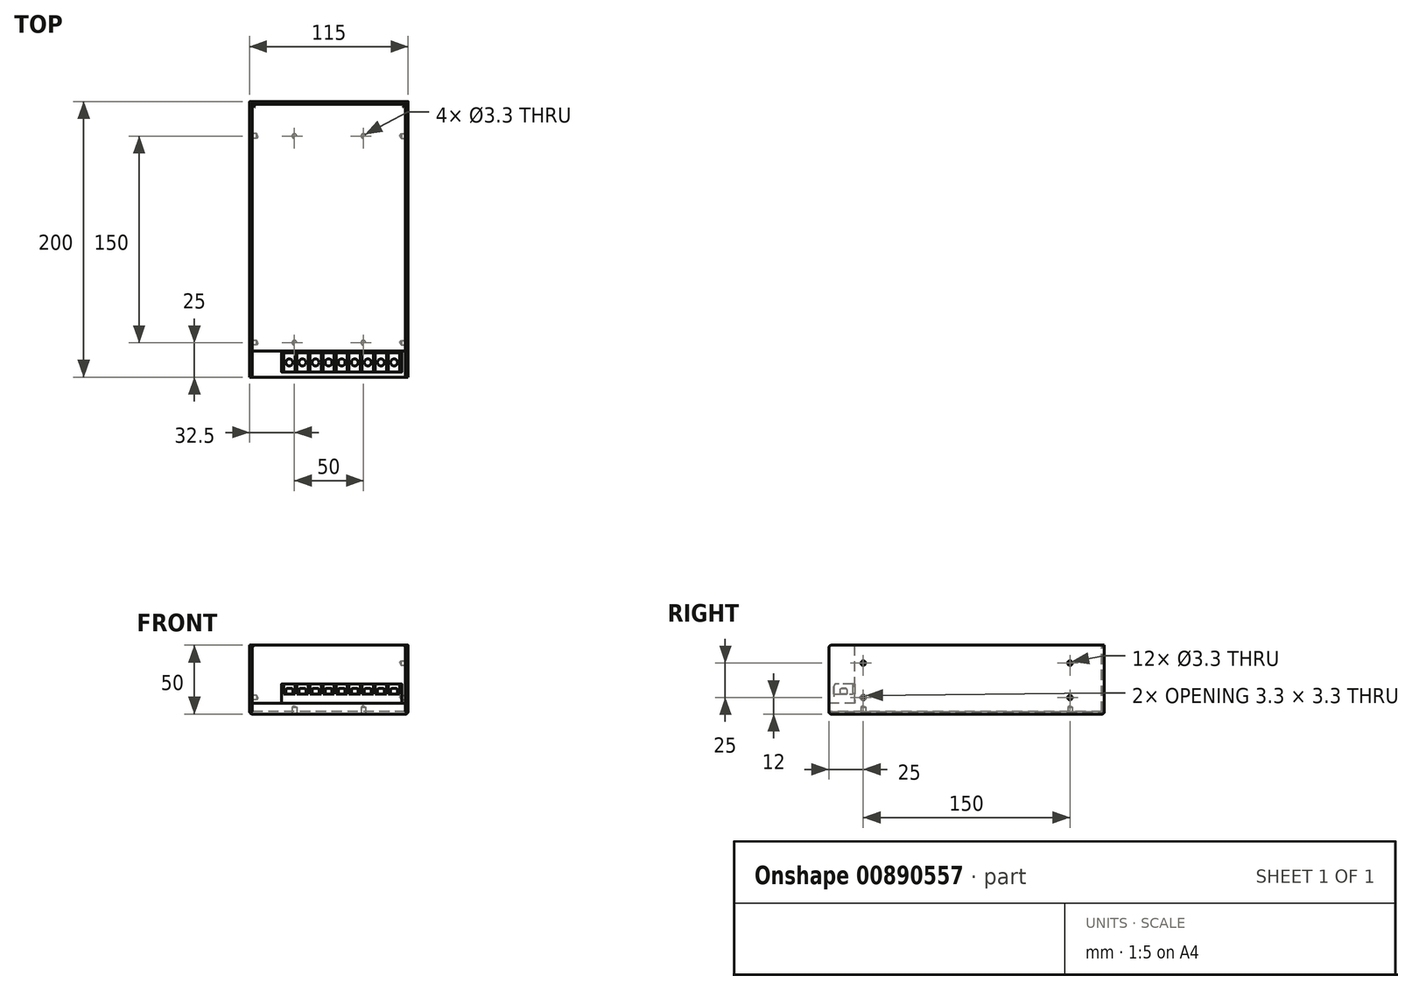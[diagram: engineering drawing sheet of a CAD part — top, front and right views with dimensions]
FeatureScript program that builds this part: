
annotation { "Feature Type Name" : "Feature", "Feature Type Description" : "" }
export const myFeature = defineFeature(function(context is Context, id is Id, definition is map)
    precondition{}
    {
        {
            var Q0;
            Q0=qCreatedBy(makeId("Front.planeOp"),FACE);
            var sketch = newSketch(context, id + "F0", { "sketchPlane" : qUnion([Q0])});
            skLineSegment(sketch, "E0.bottom", {"start": v(-57.5, 25) * mm, "end": v(0, 25) * mm});
            skLineSegment(sketch, "E0.top", {"start": v(-57.5, -25) * mm, "end": v(0, -25) * mm});
            skLineSegment(sketch, "E0.left", {"start": v(-57.5, 25) * mm, "end": v(-57.5, -25) * mm});
            skLineSegment(sketch, "E0.right", {"start": v(0, 25) * mm, "end": v(0, -25) * mm});
            skLineSegment(sketch, "E1", {"start": v(0, 0) * mm, "end": v(0, 48.13) * mm, "construction": true});
            skLineSegment(sketch, "E2", {"start": v(0, 0) * mm, "end": v(-98.9, 0) * mm, "construction": true});
            skPoint(sketch, "E2.endSnap0", {"position": v(0, 0) * mm});
            skSolve(sketch);
        }
        {
            var Q0;
            Q0=makeQuery(id+"F0.imprint","IMPRINT",FACE,{"disambiguationData":[TD([[makeQuery(id+"F0.imprint","IMPRINT",EDGE,{"derivedFrom":sQuery(id+"F0.wireOp",EDGE,"E0.bottom")}),-1.0]])]});
            extrude(context, id + "F1", {"entities" : qUnion([Q0]), "endBound" : BoundingType.SYMMETRIC, "offsetDistance" : 25 * mm, "depth" : 200 * mm});
        }
        {
            var Q0;
            Q0=makeQuery(id+"F1.opExtrude","SWEPT_FACE",FACE,{"disambiguationData":[OSD([sQuery(id+"F0.wireOp",EDGE,"E0.bottom")])]});
            var sketch = newSketch(context, id + "F2", { "sketchPlane" : qUnion([Q0])});
            skLineSegment(sketch, "E3.bottom", {"start": v(0, -100) * mm, "end": v(-55.8, -100) * mm});
            skLineSegment(sketch, "E3.top", {"start": v(0, -81) * mm, "end": v(-55.8, -81) * mm});
            skLineSegment(sketch, "E3.left", {"start": v(0, -100) * mm, "end": v(0, -81) * mm});
            skLineSegment(sketch, "E3.right", {"start": v(-55.8, -100) * mm, "end": v(-55.8, -81) * mm});
            skSolve(sketch);
        }
        {
            var Q0;
            Q0=makeQuery(id+"F2.imprint","IMPRINT",FACE,{"disambiguationData":[TD([[makeQuery(id+"F2.imprint","IMPRINT",EDGE,{"derivedFrom":sQuery(id+"F2.wireOp",EDGE,"E3.bottom")}),1.0]])]});
            extrude(context, id + "F3", {"entities" : qUnion([Q0]), "operationType" : NewBodyOperationType.REMOVE, "oppositeDirection" : true, "depth" : 42 * mm});
        }
        {
            var Q0;
            Q0=makeQuery(id+"F1.opExtrude","SWEPT_FACE",FACE,{"disambiguationData":[OSD([sQuery(id+"F0.wireOp",EDGE,"E0.bottom")])]});
            var sketch = newSketch(context, id + "F4", { "sketchPlane" : qUnion([Q0])});
            skLineSegment(sketch, "E4", {"start": v(-55.8, -100) * mm, "end": v(-55.8, 100) * mm});
            skLineSegment(sketch, "E5", {"start": v(-55.8, 100) * mm, "end": v(-55.5, 100) * mm});
            skLineSegment(sketch, "E6", {"start": v(-55.5, 100) * mm, "end": v(-55.5, 98.3) * mm});
            skLineSegment(sketch, "E7", {"start": v(-55.5, 98.3) * mm, "end": v(0, 98.3) * mm});
            skLineSegment(sketch, "E8", {"start": v(0, 98.3) * mm, "end": v(0, 98) * mm});
            skLineSegment(sketch, "E9", {"start": v(0, 98) * mm, "end": v(-55.5, 98) * mm});
            skLineSegment(sketch, "E10", {"start": v(-55.5, 98) * mm, "end": v(-55.5, -100) * mm});
            skLineSegment(sketch, "E11", {"start": v(-55.5, -100) * mm, "end": v(-55.8, -100) * mm});
            skSolve(sketch);
        }
        {
            var Q0;
            {var subQ1=sQuery(id+"F4.wireOp",EDGE,"E5");Q0=makeQuery(id+"F4.imprint","IMPRINT",FACE,{"disambiguationData":[TD([[makeQuery(id+"F4.imprint","IMPRINT",EDGE,{"derivedFrom":subQ1}),-1.0]])]});}
            var Q1;
            {var subQ0=sQuery(id+"F4.wireOp",EDGE,"E11");Q1=makeQuery(id+"F4.imprint","IMPRINT",FACE,{"disambiguationData":[TD([[makeQuery(id+"F4.imprint","IMPRINT",EDGE,{"derivedFrom":subQ0}),-1.0]])]});}
            extrude(context, id + "F5", {"entities" : qUnion([Q0, Q1]), "operationType" : NewBodyOperationType.REMOVE, "oppositeDirection" : true, "depth" : 48.3 * mm});
        }
        {
            var Q0;
            Q0=makeQuery(id+"F3.boolean.opBoolean","COPY",EDGE,{"derivedFrom":makeQuery(id+"F3.opExtrude","CAP_EDGE",EDGE,{"disambiguationData":[OSD([sQuery(id+"F2.wireOp",EDGE,"E3.top")])],"isStart":true})});
            var Q1;
            Q1=makeQuery(id+"F1.opExtrude","CAP_EDGE",EDGE,{"disambiguationData":[OSD([sQuery(id+"F0.wireOp",EDGE,"E0.top")])],"isStart":false});
            var Q2;
            Q2=makeQuery(id+"F1.opExtrude","SWEPT_EDGE",EDGE,{"disambiguationData":[OSD([sQuery(id+"F0.wireOp",EDGE,"E0.top"),sQuery(id+"F0.wireOp",EDGE,"E0.left")])]});
            var Q3;
            Q3=makeQuery(id+"F1.opExtrude","CAP_EDGE",EDGE,{"disambiguationData":[OSD([sQuery(id+"F0.wireOp",EDGE,"E0.top")])],"isStart":true});
            var Q4;
            Q4=makeQuery(id+"F1.opExtrude","CAP_EDGE",EDGE,{"disambiguationData":[OSD([sQuery(id+"F0.wireOp",EDGE,"E0.bottom")])],"isStart":false});
            var Q5;
            {var subQ0=sQuery(id+"F0.wireOp",EDGE,"E0.bottom");var subQ1=sQuery(id+"F0.wireOp",EDGE,"E0.left");Q5=makeQuery(id+"F5.boolean.opBoolean","SPLIT",EDGE,{"disambiguationData":[TD([makeQuery(id+"F1.opExtrude","SWEPT_FACE",FACE,{"disambiguationData":[OSD([subQ1])]})])],"derivedFrom":makeQuery(id+"F1.opExtrude","CAP_EDGE",EDGE,{"disambiguationData":[OSD([subQ0])],"isStart":true})});}
            var Q6;
            Q6=makeQuery(id+"F5.boolean.opBoolean","COPY",EDGE,{"derivedFrom":makeQuery(id+"F5.opExtrude","CAP_EDGE",EDGE,{"disambiguationData":[OSD([sQuery(id+"F4.wireOp",EDGE,"E6")])],"isStart":true})});
            var Q7;
            Q7=makeQuery(id+"F5.boolean.opBoolean","COPY",EDGE,{"derivedFrom":makeQuery(id+"F5.opExtrude","CAP_EDGE",EDGE,{"disambiguationData":[OSD([sQuery(id+"F4.wireOp",EDGE,"E9")])],"isStart":true})});
            var Q8;
            Q8=makeQuery(id+"F5.boolean.opBoolean","COPY",EDGE,{"derivedFrom":makeQuery(id+"F5.opExtrude","CAP_EDGE",EDGE,{"disambiguationData":[OSD([sQuery(id+"F4.wireOp",EDGE,"E10")])],"isStart":true})});
            fillet(context, id + "F6", {"entities" : qUnion([Q0, Q1, Q2, Q3, Q4, Q5, Q6, Q7, Q8]), "radius" : 2 * mm, "tangentPropagation" : true, "allowEdgeOverflow" : false});
        }
        {
            var Q0;
            Q0=makeQuery(id+"F1.opExtrude","SWEPT_BODY",BODY,{"disambiguationData":[OSD([sQuery(id+"F0.wireOp",EDGE,"E0.bottom"),sQuery(id+"F0.wireOp",EDGE,"E0.top"),sQuery(id+"F0.wireOp",EDGE,"E0.left"),sQuery(id+"F0.wireOp",EDGE,"E0.right")])]});
            var Q1;
            Q1=qCreatedBy(makeId("Right.planeOp"),FACE);
            mirror(context, id + "F7", {"operationType" : NewBodyOperationType.ADD, "entities" : qUnion([Q0]), "mirrorPlane" : qUnion([Q1])});
        }
        {
            var Q0;
            {var subQ0=makeQuery(id+"F3.boolean.opBoolean","COPY",FACE,{"derivedFrom":makeQuery(id+"F3.opExtrude","CAP_FACE",FACE,{"disambiguationData":[OSD([sQuery(id+"F2.wireOp",EDGE,"E3.bottom"),sQuery(id+"F2.wireOp",EDGE,"E3.top"),sQuery(id+"F2.wireOp",EDGE,"E3.left"),sQuery(id+"F2.wireOp",EDGE,"E3.right")])],"isStart":false})});Q0=makeQuery(id+"F7.boolean.opBoolean","MERGE",FACE,{"derivedFrom":[subQ0,makeQuery(id+"F7.opPattern","COPY",FACE,{"derivedFrom":subQ0,"instanceName":"1"})]});}
            var sketch = newSketch(context, id + "F8", { "sketchPlane" : qUnion([Q0])});
            skLineSegment(sketch, "E12.bottom", {"start": v(-34.2, -81) * mm, "end": v(52.8, -81) * mm});
            skLineSegment(sketch, "E12.top", {"start": v(-34.2, -96.3) * mm, "end": v(52.8, -96.3) * mm});
            skLineSegment(sketch, "E12.left", {"start": v(-34.2, -81) * mm, "end": v(-34.2, -96.3) * mm});
            skLineSegment(sketch, "E12.right", {"start": v(52.8, -81) * mm, "end": v(52.8, -96.3) * mm});
            skSolve(sketch);
        }
        {
            var Q0;
            Q0=makeQuery(id+"F8.imprint","IMPRINT",FACE,{"disambiguationData":[TD([[makeQuery(id+"F8.imprint","IMPRINT",EDGE,{"derivedFrom":sQuery(id+"F8.wireOp",EDGE,"E12.bottom")}),1.0]])]});
            extrude(context, id + "F9", {"entities" : qUnion([Q0]), "depth" : 14 * mm});
        }
        {
            var Q0;
            Q0=makeQuery(id+"F9.opExtrude","CAP_FACE",FACE,{"disambiguationData":[OSD([sQuery(id+"F8.wireOp",EDGE,"E12.bottom"),sQuery(id+"F8.wireOp",EDGE,"E12.top"),sQuery(id+"F8.wireOp",EDGE,"E12.left"),sQuery(id+"F8.wireOp",EDGE,"E12.right")])],"isStart":false});
            var sketch = newSketch(context, id + "F10", { "sketchPlane" : qUnion([Q0])});
            skLineSegment(sketch, "E13", {"start": v(-32.8, -96.3) * mm, "end": v(-32.8, -82.3) * mm});
            skLineSegment(sketch, "E14", {"start": v(-32.8, -82.3) * mm, "end": v(-24.6, -82.3) * mm});
            skLineSegment(sketch, "E15", {"start": v(-24.6, -82.3) * mm, "end": v(-24.6, -96.3) * mm});
            skLineSegment(sketch, "E16", {"start": v(-24.6, -96.3) * mm, "end": v(-32.8, -96.3) * mm});
            skLineSegment(sketch, "E17.1.0.0", {"start": v(-23.3, -96.3) * mm, "end": v(-23.3, -82.3) * mm});
            skLineSegment(sketch, "E17.1.0.1", {"start": v(-15.1, -96.3) * mm, "end": v(-23.3, -96.3) * mm});
            skLineSegment(sketch, "E17.1.0.2", {"start": v(-15.1, -82.3) * mm, "end": v(-15.1, -96.3) * mm});
            skLineSegment(sketch, "E17.1.0.3", {"start": v(-23.3, -82.3) * mm, "end": v(-15.1, -82.3) * mm});
            skLineSegment(sketch, "E17.2.0.0", {"start": v(-13.8, -96.3) * mm, "end": v(-13.8, -82.3) * mm});
            skLineSegment(sketch, "E17.2.0.1", {"start": v(-5.6, -96.3) * mm, "end": v(-13.8, -96.3) * mm});
            skLineSegment(sketch, "E17.2.0.2", {"start": v(-5.6, -82.3) * mm, "end": v(-5.6, -96.3) * mm});
            skLineSegment(sketch, "E17.2.0.3", {"start": v(-13.8, -82.3) * mm, "end": v(-5.6, -82.3) * mm});
            skLineSegment(sketch, "E17.3.0.0", {"start": v(-4.3, -96.3) * mm, "end": v(-4.3, -82.3) * mm});
            skLineSegment(sketch, "E17.3.0.1", {"start": v(3.9, -96.3) * mm, "end": v(-4.3, -96.3) * mm});
            skLineSegment(sketch, "E17.3.0.2", {"start": v(3.9, -82.3) * mm, "end": v(3.9, -96.3) * mm});
            skLineSegment(sketch, "E17.3.0.3", {"start": v(-4.3, -82.3) * mm, "end": v(3.9, -82.3) * mm});
            skLineSegment(sketch, "E17.4.0.0", {"start": v(5.2, -96.3) * mm, "end": v(5.2, -82.3) * mm});
            skLineSegment(sketch, "E17.4.0.1", {"start": v(13.4, -96.3) * mm, "end": v(5.2, -96.3) * mm});
            skLineSegment(sketch, "E17.4.0.2", {"start": v(13.4, -82.3) * mm, "end": v(13.4, -96.3) * mm});
            skLineSegment(sketch, "E17.4.0.3", {"start": v(5.2, -82.3) * mm, "end": v(13.4, -82.3) * mm});
            skLineSegment(sketch, "E17.5.0.0", {"start": v(14.7, -96.3) * mm, "end": v(14.7, -82.3) * mm});
            skLineSegment(sketch, "E17.5.0.1", {"start": v(22.9, -96.3) * mm, "end": v(14.7, -96.3) * mm});
            skLineSegment(sketch, "E17.5.0.2", {"start": v(22.9, -82.3) * mm, "end": v(22.9, -96.3) * mm});
            skLineSegment(sketch, "E17.5.0.3", {"start": v(14.7, -82.3) * mm, "end": v(22.9, -82.3) * mm});
            skLineSegment(sketch, "E17.6.0.0", {"start": v(24.2, -96.3) * mm, "end": v(24.2, -82.3) * mm});
            skLineSegment(sketch, "E17.6.0.1", {"start": v(32.4, -96.3) * mm, "end": v(24.2, -96.3) * mm});
            skLineSegment(sketch, "E17.6.0.2", {"start": v(32.4, -82.3) * mm, "end": v(32.4, -96.3) * mm});
            skLineSegment(sketch, "E17.6.0.3", {"start": v(24.2, -82.3) * mm, "end": v(32.4, -82.3) * mm});
            skLineSegment(sketch, "E17.7.0.0", {"start": v(33.7, -96.3) * mm, "end": v(33.7, -82.3) * mm});
            skLineSegment(sketch, "E17.7.0.1", {"start": v(41.9, -96.3) * mm, "end": v(33.7, -96.3) * mm});
            skLineSegment(sketch, "E17.7.0.2", {"start": v(41.9, -82.3) * mm, "end": v(41.9, -96.3) * mm});
            skLineSegment(sketch, "E17.7.0.3", {"start": v(33.7, -82.3) * mm, "end": v(41.9, -82.3) * mm});
            skLineSegment(sketch, "E17.8.0.0", {"start": v(43.2, -96.3) * mm, "end": v(43.2, -82.3) * mm});
            skLineSegment(sketch, "E17.8.0.1", {"start": v(51.4, -96.3) * mm, "end": v(43.2, -96.3) * mm});
            skLineSegment(sketch, "E17.8.0.2", {"start": v(51.4, -82.3) * mm, "end": v(51.4, -96.3) * mm});
            skLineSegment(sketch, "E17.8.0.3", {"start": v(43.2, -82.3) * mm, "end": v(51.4, -82.3) * mm});
            skLineSegment(sketch, "E17.direction1", {"start": v(-32.8, -96.3) * mm, "end": v(-23.3, -96.3) * mm, "construction": true});
            skSolve(sketch);
        }
        {
            var Q0;
            Q0=makeQuery(id+"F10.imprint","IMPRINT",FACE,{"disambiguationData":[TD([[makeQuery(id+"F10.imprint","IMPRINT",EDGE,{"derivedFrom":sQuery(id+"F10.wireOp",EDGE,"E13")}),-1.0]])]});
            var Q1;
            Q1=makeQuery(id+"F10.imprint","IMPRINT",FACE,{"disambiguationData":[TD([[makeQuery(id+"F10.imprint","IMPRINT",EDGE,{"derivedFrom":sQuery(id+"F10.wireOp",EDGE,"E17.1.0.0")}),-1.0]])]});
            var Q2;
            Q2=makeQuery(id+"F10.imprint","IMPRINT",FACE,{"disambiguationData":[TD([[makeQuery(id+"F10.imprint","IMPRINT",EDGE,{"derivedFrom":sQuery(id+"F10.wireOp",EDGE,"E17.2.0.0")}),-1.0]])]});
            var Q3;
            Q3=makeQuery(id+"F10.imprint","IMPRINT",FACE,{"disambiguationData":[TD([[makeQuery(id+"F10.imprint","IMPRINT",EDGE,{"derivedFrom":sQuery(id+"F10.wireOp",EDGE,"E17.3.0.0")}),-1.0]])]});
            var Q4;
            Q4=makeQuery(id+"F10.imprint","IMPRINT",FACE,{"disambiguationData":[TD([[makeQuery(id+"F10.imprint","IMPRINT",EDGE,{"derivedFrom":sQuery(id+"F10.wireOp",EDGE,"E17.4.0.0")}),-1.0]])]});
            var Q5;
            Q5=makeQuery(id+"F10.imprint","IMPRINT",FACE,{"disambiguationData":[TD([[makeQuery(id+"F10.imprint","IMPRINT",EDGE,{"derivedFrom":sQuery(id+"F10.wireOp",EDGE,"E17.5.0.0")}),-1.0]])]});
            var Q6;
            Q6=makeQuery(id+"F10.imprint","IMPRINT",FACE,{"disambiguationData":[TD([[makeQuery(id+"F10.imprint","IMPRINT",EDGE,{"derivedFrom":sQuery(id+"F10.wireOp",EDGE,"E17.6.0.0")}),-1.0]])]});
            var Q7;
            Q7=makeQuery(id+"F10.imprint","IMPRINT",FACE,{"disambiguationData":[TD([[makeQuery(id+"F10.imprint","IMPRINT",EDGE,{"derivedFrom":sQuery(id+"F10.wireOp",EDGE,"E17.7.0.0")}),-1.0]])]});
            var Q8;
            Q8=makeQuery(id+"F10.imprint","IMPRINT",FACE,{"disambiguationData":[TD([[makeQuery(id+"F10.imprint","IMPRINT",EDGE,{"derivedFrom":sQuery(id+"F10.wireOp",EDGE,"E17.8.0.0")}),-1.0]])]});
            extrude(context, id + "F11", {"entities" : qUnion([Q0, Q1, Q2, Q3, Q4, Q5, Q6, Q7, Q8]), "operationType" : NewBodyOperationType.REMOVE, "oppositeDirection" : true, "depth" : 7.4 * mm});
        }
        {
            var Q0;
            {var subQ0=sQuery(id+"F8.wireOp",EDGE,"E12.left");var subQ1=sQuery(id+"F8.wireOp",EDGE,"E12.top");Q0=makeQuery(id+"F11.boolean.opBoolean","SPLIT",EDGE,{"disambiguationData":[TD([makeQuery(id+"F9.opExtrude","SWEPT_FACE",FACE,{"disambiguationData":[OSD([subQ0])]})])],"derivedFrom":makeQuery(id+"F9.opExtrude","CAP_EDGE",EDGE,{"disambiguationData":[OSD([subQ1])],"isStart":false})});}
            var Q1;
            {var subQ0=sQuery(id+"F8.wireOp",EDGE,"E12.top");Q1=makeQuery(id+"F11.boolean.opBoolean","SPLIT",EDGE,{"disambiguationData":[TD([makeQuery(id+"F11.opExtrude","SWEPT_FACE",FACE,{"disambiguationData":[OSD([sQuery(id+"F10.wireOp",EDGE,"E15")])]})])],"derivedFrom":makeQuery(id+"F9.opExtrude","CAP_EDGE",EDGE,{"disambiguationData":[OSD([subQ0])],"isStart":false})});}
            var Q2;
            {var subQ0=sQuery(id+"F8.wireOp",EDGE,"E12.top");Q2=makeQuery(id+"F11.boolean.opBoolean","SPLIT",EDGE,{"disambiguationData":[TD([makeQuery(id+"F11.opExtrude","SWEPT_FACE",FACE,{"disambiguationData":[OSD([sQuery(id+"F10.wireOp",EDGE,"E17.1.0.2")])]})])],"derivedFrom":makeQuery(id+"F9.opExtrude","CAP_EDGE",EDGE,{"disambiguationData":[OSD([subQ0])],"isStart":false})});}
            var Q3;
            {var subQ0=sQuery(id+"F8.wireOp",EDGE,"E12.top");Q3=makeQuery(id+"F11.boolean.opBoolean","SPLIT",EDGE,{"disambiguationData":[TD([makeQuery(id+"F11.opExtrude","SWEPT_FACE",FACE,{"disambiguationData":[OSD([sQuery(id+"F10.wireOp",EDGE,"E17.2.0.2")])]})])],"derivedFrom":makeQuery(id+"F9.opExtrude","CAP_EDGE",EDGE,{"disambiguationData":[OSD([subQ0])],"isStart":false})});}
            var Q4;
            {var subQ0=sQuery(id+"F8.wireOp",EDGE,"E12.top");Q4=makeQuery(id+"F11.boolean.opBoolean","SPLIT",EDGE,{"disambiguationData":[TD([makeQuery(id+"F11.opExtrude","SWEPT_FACE",FACE,{"disambiguationData":[OSD([sQuery(id+"F10.wireOp",EDGE,"E17.3.0.2")])]})])],"derivedFrom":makeQuery(id+"F9.opExtrude","CAP_EDGE",EDGE,{"disambiguationData":[OSD([subQ0])],"isStart":false})});}
            var Q5;
            {var subQ0=sQuery(id+"F8.wireOp",EDGE,"E12.top");Q5=makeQuery(id+"F11.boolean.opBoolean","SPLIT",EDGE,{"disambiguationData":[TD([makeQuery(id+"F11.opExtrude","SWEPT_FACE",FACE,{"disambiguationData":[OSD([sQuery(id+"F10.wireOp",EDGE,"E17.4.0.2")])]})])],"derivedFrom":makeQuery(id+"F9.opExtrude","CAP_EDGE",EDGE,{"disambiguationData":[OSD([subQ0])],"isStart":false})});}
            var Q6;
            {var subQ0=sQuery(id+"F8.wireOp",EDGE,"E12.top");Q6=makeQuery(id+"F11.boolean.opBoolean","SPLIT",EDGE,{"disambiguationData":[TD([makeQuery(id+"F11.opExtrude","SWEPT_FACE",FACE,{"disambiguationData":[OSD([sQuery(id+"F10.wireOp",EDGE,"E17.5.0.2")])]})])],"derivedFrom":makeQuery(id+"F9.opExtrude","CAP_EDGE",EDGE,{"disambiguationData":[OSD([subQ0])],"isStart":false})});}
            var Q7;
            {var subQ0=sQuery(id+"F8.wireOp",EDGE,"E12.top");Q7=makeQuery(id+"F11.boolean.opBoolean","SPLIT",EDGE,{"disambiguationData":[TD([makeQuery(id+"F11.opExtrude","SWEPT_FACE",FACE,{"disambiguationData":[OSD([sQuery(id+"F10.wireOp",EDGE,"E17.6.0.2")])]})])],"derivedFrom":makeQuery(id+"F9.opExtrude","CAP_EDGE",EDGE,{"disambiguationData":[OSD([subQ0])],"isStart":false})});}
            var Q8;
            {var subQ0=sQuery(id+"F8.wireOp",EDGE,"E12.top");Q8=makeQuery(id+"F11.boolean.opBoolean","SPLIT",EDGE,{"disambiguationData":[TD([makeQuery(id+"F11.opExtrude","SWEPT_FACE",FACE,{"disambiguationData":[OSD([sQuery(id+"F10.wireOp",EDGE,"E17.7.0.2")])]})])],"derivedFrom":makeQuery(id+"F9.opExtrude","CAP_EDGE",EDGE,{"disambiguationData":[OSD([subQ0])],"isStart":false})});}
            var Q9;
            {var subQ0=sQuery(id+"F8.wireOp",EDGE,"E12.right");var subQ1=sQuery(id+"F8.wireOp",EDGE,"E12.top");Q9=makeQuery(id+"F11.boolean.opBoolean","SPLIT",EDGE,{"disambiguationData":[TD([makeQuery(id+"F9.opExtrude","SWEPT_FACE",FACE,{"disambiguationData":[OSD([subQ0])]})])],"derivedFrom":makeQuery(id+"F9.opExtrude","CAP_EDGE",EDGE,{"disambiguationData":[OSD([subQ1])],"isStart":false})});}
            fillet(context, id + "F12", {"entities" : qUnion([Q0, Q1, Q2, Q3, Q4, Q5, Q6, Q7, Q8, Q9]), "radius" : 2 * mm, "tangentPropagation" : true, "allowEdgeOverflow" : false});
        }
        {
            var Q0;
            Q0=makeQuery(id+"F11.boolean.opBoolean","COPY",FACE,{"derivedFrom":makeQuery(id+"F11.opExtrude","CAP_FACE",FACE,{"disambiguationData":[OSD([sQuery(id+"F10.wireOp",EDGE,"E13"),sQuery(id+"F10.wireOp",EDGE,"E14"),sQuery(id+"F10.wireOp",EDGE,"E15"),sQuery(id+"F10.wireOp",EDGE,"E16")])],"isStart":false})});
            var sketch = newSketch(context, id + "F13", { "sketchPlane" : qUnion([Q0])});
            skLineSegment(sketch, "E18", {"start": v(-32.8, -82.3) * mm, "end": v(-24.6, -96.3) * mm, "construction": true});
            skCircle(sketch, "E19", {"center": v(-28.7, -89.3) * mm, "radius": 2.5 * mm});
            skCircle(sketch, "E20.1.0.0", {"center": v(-19.2, -89.3) * mm, "radius": 2.5 * mm});
            skCircle(sketch, "E20.2.0.0", {"center": v(-9.7, -89.3) * mm, "radius": 2.5 * mm});
            skCircle(sketch, "E20.3.0.0", {"center": v(-0.2, -89.3) * mm, "radius": 2.5 * mm});
            skCircle(sketch, "E20.4.0.0", {"center": v(9.3, -89.3) * mm, "radius": 2.5 * mm});
            skCircle(sketch, "E20.5.0.0", {"center": v(18.8, -89.3) * mm, "radius": 2.5 * mm});
            skCircle(sketch, "E20.6.0.0", {"center": v(28.3, -89.3) * mm, "radius": 2.5 * mm});
            skCircle(sketch, "E20.7.0.0", {"center": v(37.8, -89.3) * mm, "radius": 2.5 * mm});
            skCircle(sketch, "E20.8.0.0", {"center": v(47.3, -89.3) * mm, "radius": 2.5 * mm});
            skLineSegment(sketch, "E20.direction1", {"start": v(-28.7, -89.3) * mm, "end": v(-19.2, -89.3) * mm, "construction": true});
            skSolve(sketch);
        }
        {
            var Q0;
            Q0=makeQuery(id+"F13.imprint","IMPRINT",FACE,{"disambiguationData":[TD([[makeQuery(id+"F13.imprint","IMPRINT",EDGE,{"derivedFrom":sQuery(id+"F13.wireOp",EDGE,"E19")}),1.0]])]});
            var Q1;
            Q1=makeQuery(id+"F13.imprint","IMPRINT",FACE,{"disambiguationData":[TD([[makeQuery(id+"F13.imprint","IMPRINT",EDGE,{"derivedFrom":sQuery(id+"F13.wireOp",EDGE,"E20.1.0.0")}),1.0]])]});
            var Q2;
            Q2=makeQuery(id+"F13.imprint","IMPRINT",FACE,{"disambiguationData":[TD([[makeQuery(id+"F13.imprint","IMPRINT",EDGE,{"derivedFrom":sQuery(id+"F13.wireOp",EDGE,"E20.2.0.0")}),1.0]])]});
            var Q3;
            Q3=makeQuery(id+"F13.imprint","IMPRINT",FACE,{"disambiguationData":[TD([[makeQuery(id+"F13.imprint","IMPRINT",EDGE,{"derivedFrom":sQuery(id+"F13.wireOp",EDGE,"E20.3.0.0")}),1.0]])]});
            var Q4;
            Q4=makeQuery(id+"F13.imprint","IMPRINT",FACE,{"disambiguationData":[TD([[makeQuery(id+"F13.imprint","IMPRINT",EDGE,{"derivedFrom":sQuery(id+"F13.wireOp",EDGE,"E20.4.0.0")}),1.0]])]});
            var Q5;
            Q5=makeQuery(id+"F13.imprint","IMPRINT",FACE,{"disambiguationData":[TD([[makeQuery(id+"F13.imprint","IMPRINT",EDGE,{"derivedFrom":sQuery(id+"F13.wireOp",EDGE,"E20.5.0.0")}),1.0]])]});
            var Q6;
            Q6=makeQuery(id+"F13.imprint","IMPRINT",FACE,{"disambiguationData":[TD([[makeQuery(id+"F13.imprint","IMPRINT",EDGE,{"derivedFrom":sQuery(id+"F13.wireOp",EDGE,"E20.6.0.0")}),1.0]])]});
            var Q7;
            Q7=makeQuery(id+"F13.imprint","IMPRINT",FACE,{"disambiguationData":[TD([[makeQuery(id+"F13.imprint","IMPRINT",EDGE,{"derivedFrom":sQuery(id+"F13.wireOp",EDGE,"E20.7.0.0")}),1.0]])]});
            var Q8;
            Q8=makeQuery(id+"F13.imprint","IMPRINT",FACE,{"disambiguationData":[TD([[makeQuery(id+"F13.imprint","IMPRINT",EDGE,{"derivedFrom":sQuery(id+"F13.wireOp",EDGE,"E20.8.0.0")}),1.0]])]});
            var Q9;
            Q9=sQuery(id+"F13.wireOp",EDGE,"E19");
            extrude(context, id + "F14", {"entities" : qUnion([Q0, Q1, Q2, Q3, Q4, Q5, Q6, Q7, Q8]), "operationType" : NewBodyOperationType.ADD, "surfaceEntities" : qUnion([Q9]), "depth" : 4 * mm});
        }
        {
            var Q0;
            Q0=makeQuery(id+"F14.opExtrude","CAP_EDGE",EDGE,{"disambiguationData":[OSD([sQuery(id+"F13.wireOp",EDGE,"E19")])],"isStart":false});
            var Q1;
            Q1=makeQuery(id+"F14.opExtrude","CAP_EDGE",EDGE,{"disambiguationData":[OSD([sQuery(id+"F13.wireOp",EDGE,"E20.1.0.0")])],"isStart":false});
            var Q2;
            Q2=makeQuery(id+"F14.opExtrude","CAP_EDGE",EDGE,{"disambiguationData":[OSD([sQuery(id+"F13.wireOp",EDGE,"E20.2.0.0")])],"isStart":false});
            var Q3;
            Q3=makeQuery(id+"F14.opExtrude","CAP_EDGE",EDGE,{"disambiguationData":[OSD([sQuery(id+"F13.wireOp",EDGE,"E20.3.0.0")])],"isStart":false});
            var Q4;
            Q4=makeQuery(id+"F14.opExtrude","CAP_EDGE",EDGE,{"disambiguationData":[OSD([sQuery(id+"F13.wireOp",EDGE,"E20.4.0.0")])],"isStart":false});
            var Q5;
            Q5=makeQuery(id+"F14.opExtrude","CAP_EDGE",EDGE,{"disambiguationData":[OSD([sQuery(id+"F13.wireOp",EDGE,"E20.5.0.0")])],"isStart":false});
            var Q6;
            Q6=makeQuery(id+"F14.opExtrude","CAP_EDGE",EDGE,{"disambiguationData":[OSD([sQuery(id+"F13.wireOp",EDGE,"E20.6.0.0")])],"isStart":false});
            var Q7;
            Q7=makeQuery(id+"F14.opExtrude","CAP_EDGE",EDGE,{"disambiguationData":[OSD([sQuery(id+"F13.wireOp",EDGE,"E20.7.0.0")])],"isStart":false});
            var Q8;
            Q8=makeQuery(id+"F14.opExtrude","CAP_EDGE",EDGE,{"disambiguationData":[OSD([sQuery(id+"F13.wireOp",EDGE,"E20.8.0.0")])],"isStart":false});
            fillet(context, id + "F15", {"entities" : qUnion([Q0, Q1, Q2, Q3, Q4, Q5, Q6, Q7, Q8]), "radius" : 1 * mm, "tangentPropagation" : true, "allowEdgeOverflow" : false});
        }
        {
            var Q0;
            Q0=makeQuery(id+"F1.opExtrude","SWEPT_FACE",FACE,{"disambiguationData":[OSD([sQuery(id+"F0.wireOp",EDGE,"E0.left")])]});
            var sketch = newSketch(context, id + "F16", { "sketchPlane" : qUnion([Q0])});
            skLineSegment(sketch, "E21", {"start": v(-75, -13) * mm, "end": v(75, -13) * mm});
            skLineSegment(sketch, "E22", {"start": v(0, 0) * mm, "end": v(0, -13) * mm});
            skSolve(sketch);
        }
        {
            var Q0;
            Q0=makeQuery(id+"F7.opPattern","COPY",FACE,{"derivedFrom":makeQuery(id+"F1.opExtrude","SWEPT_FACE",FACE,{"disambiguationData":[OSD([sQuery(id+"F0.wireOp",EDGE,"E0.left")])]}),"instanceName":"1"});
            var sketch = newSketch(context, id + "F17", { "sketchPlane" : qUnion([Q0])});
            skPoint(sketch, "E23.0", {"position": v(-75, -13) * mm});
            skPoint(sketch, "E23.1", {"position": v(75, -13) * mm});
            skPoint(sketch, "E24", {"position": v(-75, 12) * mm});
            skPoint(sketch, "E25", {"position": v(75, 12) * mm});
            skSolve(sketch);
        }
        {
            var Q0;
            {var subQ0=makeQuery(id+"F1.opExtrude","SWEPT_FACE",FACE,{"disambiguationData":[OSD([sQuery(id+"F0.wireOp",EDGE,"E0.top")])]});Q0=makeQuery(id+"F7.boolean.opBoolean","MERGE",FACE,{"derivedFrom":[subQ0,makeQuery(id+"F7.opPattern","COPY",FACE,{"derivedFrom":subQ0,"instanceName":"1"})]});}
            var sketch = newSketch(context, id + "F18", { "sketchPlane" : qUnion([Q0])});
            skLineSegment(sketch, "E26", {"start": v(-21.97, 0) * mm, "end": v(0, 0) * mm, "construction": true});
            skLineSegment(sketch, "E27", {"start": v(0, 0) * mm, "end": v(0, 32.91) * mm, "construction": true});
            skPoint(sketch, "E28", {"position": v(-25, 75) * mm});
            skPoint(sketch, "E29.MirrorP", {"position": v(-25, -75) * mm});
            skPoint(sketch, "E30.MirrorP", {"position": v(25, -75) * mm});
            skPoint(sketch, "E31.MirrorP", {"position": v(25, 75) * mm});
            skSolve(sketch);
        }
        {
            var Q0;
            Q0=sQuery(id+"F16.wireOp",VERTEX,"E21.start");
            var Q1;
            Q1=sQuery(id+"F16.wireOp",VERTEX,"E21.end");
            var Q2;
            Q2=sQuery(id+"F18.wireOp",VERTEX,"E29.MirrorP");
            var Q3;
            Q3=sQuery(id+"F18.wireOp",VERTEX,"E28");
            var Q4;
            Q4=sQuery(id+"F18.wireOp",VERTEX,"E30.MirrorP");
            var Q5;
            Q5=sQuery(id+"F18.wireOp",VERTEX,"E31.MirrorP");
            var Q6;
            Q6=sQuery(id+"F17.wireOp",VERTEX,"E23.0");
            var Q7;
            Q7=sQuery(id+"F17.wireOp",VERTEX,"E24");
            var Q8;
            Q8=sQuery(id+"F17.wireOp",VERTEX,"E25");
            var Q9;
            Q9=sQuery(id+"F17.wireOp",VERTEX,"E23.1");
            var Q10;
            Q10=makeQuery(id+"F1.opExtrude","SWEPT_BODY",BODY,{"disambiguationData":[OSD([sQuery(id+"F0.wireOp",EDGE,"E0.bottom"),sQuery(id+"F0.wireOp",EDGE,"E0.top"),sQuery(id+"F0.wireOp",EDGE,"E0.left"),sQuery(id+"F0.wireOp",EDGE,"E0.right")])]});
            hole(context, id + "F19", {"style" : HoleStyle.SIMPLE, "endStyle" : HoleEndStyle.BLIND, "holeDiameter" : 3.3 * mm, "holeDepth" : 5 * mm, "locations" : qUnion([Q0, Q1, Q2, Q3, Q4, Q5, Q6, Q7, Q8, Q9]), "scope" : qUnion([Q10])});
        }
    });
